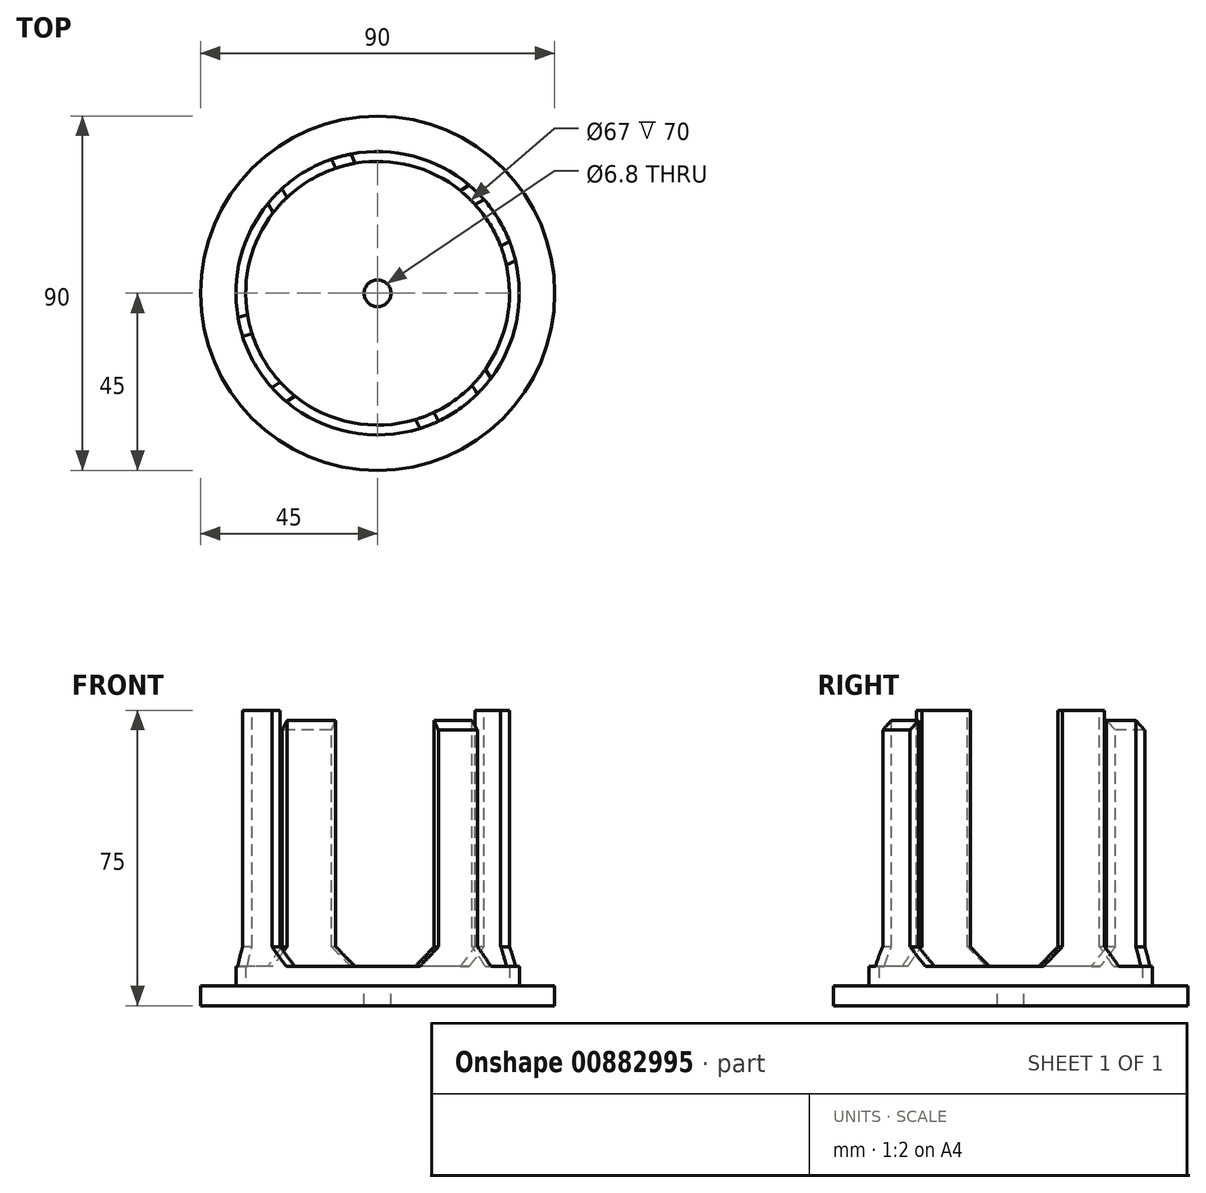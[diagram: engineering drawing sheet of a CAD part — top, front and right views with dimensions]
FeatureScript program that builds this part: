
annotation { "Feature Type Name" : "Feature", "Feature Type Description" : "" }
export const myFeature = defineFeature(function(context is Context, id is Id, definition is map)
    precondition{}
    {
        {
            var Q0;
            Q0=qCreatedBy(makeId("Top.planeOp"),FACE);
            var sketch = newSketch(context, id + "F0", { "sketchPlane" : qUnion([Q0])});
            skCircle(sketch, "E0", {"center": v(0, 0) * mm, "radius": 45 * mm});
            skSolve(sketch);
        }
        {
            var Q0;
            Q0 = qSketchRegion(id + "F0", true);
            extrude(context, id + "F1", {"entities" : qUnion([Q0]), "depth" : 5 * mm, "offsetDistance" : 25 * mm});
        }
        {
            var Q0;
            Q0=makeQuery(id+"F1.opExtrude","CAP_FACE",FACE,{"disambiguationData":[OSD([sQuery(id+"F0.wireOp",EDGE,"E0")])],"isStart":false});
            var sketch = newSketch(context, id + "F2", { "sketchPlane" : qUnion([Q0])});
            skCircle(sketch, "E1", {"center": v(0, 0) * mm, "radius": 36 * mm});
            skCircle(sketch, "E2", {"center": v(0, 0) * mm, "radius": 33.5 * mm});
            skSolve(sketch);
        }
        {
            var Q0;
            Q0=makeQuery(id+"F2.imprint","IMPRINT",FACE,{"disambiguationData":[TD([[makeQuery(id+"F2.imprint","IMPRINT",EDGE,{"derivedFrom":sQuery(id+"F2.wireOp",EDGE,"E1")}),1.0]])]});
            extrude(context, id + "F3", {"entities" : qUnion([Q0]), "operationType" : NewBodyOperationType.ADD, "depth" : 70 * mm, "offsetDistance" : 25 * mm});
        }
        {
            var Q0;
            Q0=makeQuery(id+"F3.opExtrude","CAP_FACE",FACE,{"disambiguationData":[OSD([sQuery(id+"F2.wireOp",EDGE,"E1"),sQuery(id+"F2.wireOp",EDGE,"E2")])],"isStart":false});
            var sketch = newSketch(context, id + "F4", { "sketchPlane" : qUnion([Q0])});
            skLineSegment(sketch, "E3", {"start": v(-24.29, 26.57) * mm, "end": v(-23, 24.36) * mm});
            skLineSegment(sketch, "E4", {"start": v(-11.71, 34.04) * mm, "end": v(-10.63, 31.77) * mm});
            skLineSegment(sketch, "E5", {"start": v(24, -23.38) * mm, "end": v(25.35, -25.56) * mm});
            skLineSegment(sketch, "E6", {"start": v(14.33, -30.28) * mm, "end": v(15.46, -32.51) * mm});
            skLineSegment(sketch, "E7", {"start": v(24.8, 22.52) * mm, "end": v(26.98, 23.84) * mm});
            skLineSegment(sketch, "E8", {"start": v(31.27, 12.01) * mm, "end": v(33.52, 13.12) * mm});
            skLineSegment(sketch, "E9", {"start": v(-31.88, -10.28) * mm, "end": v(-34.28, -11) * mm});
            skLineSegment(sketch, "E10", {"start": v(-24.74, -22.59) * mm, "end": v(-26.84, -24) * mm});
            skSolve(sketch);
        }
        {
            var Q0;
            {var subQ0=sQuery(id+"F4.wireOp",EDGE,"E3");Q0=makeQuery(id+"F4.imprint","IMPRINT",FACE,{"disambiguationData":[TD([[makeQuery(id+"F4.imprint","IMPRINT",EDGE,{"derivedFrom":subQ0}),-1.0]])]});}
            var Q1;
            {var subQ0=sQuery(id+"F4.wireOp",EDGE,"E4");Q1=makeQuery(id+"F4.imprint","IMPRINT",FACE,{"disambiguationData":[TD([[makeQuery(id+"F4.imprint","IMPRINT",EDGE,{"derivedFrom":subQ0}),1.0]])]});}
            var Q2;
            {var subQ0=sQuery(id+"F4.wireOp",EDGE,"E5");Q2=makeQuery(id+"F4.imprint","IMPRINT",FACE,{"disambiguationData":[TD([[makeQuery(id+"F4.imprint","IMPRINT",EDGE,{"derivedFrom":subQ0}),1.0]])]});}
            var Q3;
            {var subQ0=sQuery(id+"F4.wireOp",EDGE,"E6");Q3=makeQuery(id+"F4.imprint","IMPRINT",FACE,{"disambiguationData":[TD([[makeQuery(id+"F4.imprint","IMPRINT",EDGE,{"derivedFrom":subQ0}),-1.0]])]});}
            extrude(context, id + "F5", {"entities" : qUnion([Q0, Q1, Q2, Q3]), "operationType" : NewBodyOperationType.REMOVE, "oppositeDirection" : true, "depth" : 65 * mm, "offsetDistance" : 25 * mm});
        }
        {
            var Q0;
            Q0=makeQuery(id+"F3.boolean.opBoolean","SPLIT",FACE,{"disambiguationData":[TD([makeQuery(id+"F3.opExtrude","SWEPT_FACE",FACE,{"disambiguationData":[OSD([sQuery(id+"F2.wireOp",EDGE,"E2")])]})])],"derivedFrom":makeQuery(id+"F1.opExtrude","CAP_FACE",FACE,{"disambiguationData":[OSD([sQuery(id+"F0.wireOp",EDGE,"E0")])],"isStart":false})});
            var sketch = newSketch(context, id + "F6", { "sketchPlane" : qUnion([Q0])});
            skCircle(sketch, "E11", {"center": v(0, 0) * mm, "radius": 3.4 * mm});
            skSolve(sketch);
        }
        {
            var Q0;
            Q0 = qSketchRegion(id + "F6", true);
            extrude(context, id + "F7", {"entities" : qUnion([Q0]), "operationType" : NewBodyOperationType.REMOVE, "endBound" : BoundingType.THROUGH_ALL, "oppositeDirection" : true, "depth" : 25 * mm, "offsetDistance" : 25 * mm});
        }
        {
            var Q0;
            {var subQ0=sQuery(id+"F2.wireOp",EDGE,"E1");Q0=makeQuery(id+"F5.boolean.opBoolean","SPLIT",EDGE,{"disambiguationData":[TD([makeQuery(id+"F5.opExtrude","SWEPT_FACE",FACE,{"disambiguationData":[OSD([sQuery(id+"F4.wireOp",EDGE,"E3")])]})])],"derivedFrom":makeQuery(id+"F3.opExtrude","CAP_EDGE",EDGE,{"disambiguationData":[OSD([subQ0])],"isStart":false})});}
            var Q1;
            {var subQ0=sQuery(id+"F2.wireOp",EDGE,"E1");Q1=makeQuery(id+"F5.boolean.opBoolean","SPLIT",EDGE,{"disambiguationData":[TD([makeQuery(id+"F5.opExtrude","SWEPT_FACE",FACE,{"disambiguationData":[OSD([sQuery(id+"F4.wireOp",EDGE,"E4")])]})])],"derivedFrom":makeQuery(id+"F3.opExtrude","CAP_EDGE",EDGE,{"disambiguationData":[OSD([subQ0])],"isStart":false})});}
            var Q2;
            {var subQ0=sQuery(id+"F2.wireOp",EDGE,"E1");Q2=makeQuery(id+"F5.boolean.opBoolean","SPLIT",EDGE,{"disambiguationData":[TD([makeQuery(id+"F5.opExtrude","SWEPT_FACE",FACE,{"disambiguationData":[OSD([sQuery(id+"F4.wireOp",EDGE,"E5")])]})])],"derivedFrom":makeQuery(id+"F3.opExtrude","CAP_EDGE",EDGE,{"disambiguationData":[OSD([subQ0])],"isStart":false})});}
            var Q3;
            {var subQ0=sQuery(id+"F2.wireOp",EDGE,"E1");Q3=makeQuery(id+"F5.boolean.opBoolean","SPLIT",EDGE,{"disambiguationData":[TD([makeQuery(id+"F5.opExtrude","SWEPT_FACE",FACE,{"disambiguationData":[OSD([sQuery(id+"F4.wireOp",EDGE,"E6")])]})])],"derivedFrom":makeQuery(id+"F3.opExtrude","CAP_EDGE",EDGE,{"disambiguationData":[OSD([subQ0])],"isStart":false})});}
            chamfer(context, id + "F8", {"entities" : qUnion([Q0, Q1, Q2, Q3]), "width" : 5 * mm, "tangentPropagation" : true});
        }
        {
            var Q0;
            Q0=makeQuery(id+"F5.boolean.opBoolean","COPY",EDGE,{"derivedFrom":makeQuery(id+"F5.opExtrude","CAP_EDGE",EDGE,{"disambiguationData":[OSD([sQuery(id+"F4.wireOp",EDGE,"E3")])],"isStart":false})});
            var Q1;
            Q1=makeQuery(id+"F5.boolean.opBoolean","COPY",EDGE,{"derivedFrom":makeQuery(id+"F5.opExtrude","CAP_EDGE",EDGE,{"disambiguationData":[OSD([sQuery(id+"F4.wireOp",EDGE,"E4")])],"isStart":false})});
            var Q2;
            Q2=makeQuery(id+"F5.boolean.opBoolean","COPY",EDGE,{"derivedFrom":makeQuery(id+"F5.opExtrude","CAP_EDGE",EDGE,{"disambiguationData":[OSD([sQuery(id+"F4.wireOp",EDGE,"E7")])],"isStart":false})});
            var Q3;
            Q3=makeQuery(id+"F5.boolean.opBoolean","COPY",EDGE,{"derivedFrom":makeQuery(id+"F5.opExtrude","CAP_EDGE",EDGE,{"disambiguationData":[OSD([sQuery(id+"F4.wireOp",EDGE,"E8")])],"isStart":false})});
            var Q4;
            Q4=makeQuery(id+"F5.boolean.opBoolean","COPY",EDGE,{"derivedFrom":makeQuery(id+"F5.opExtrude","CAP_EDGE",EDGE,{"disambiguationData":[OSD([sQuery(id+"F4.wireOp",EDGE,"E5")])],"isStart":false})});
            var Q5;
            Q5=makeQuery(id+"F5.boolean.opBoolean","COPY",EDGE,{"derivedFrom":makeQuery(id+"F5.opExtrude","CAP_EDGE",EDGE,{"disambiguationData":[OSD([sQuery(id+"F4.wireOp",EDGE,"E6")])],"isStart":false})});
            var Q6;
            Q6=makeQuery(id+"F5.boolean.opBoolean","COPY",EDGE,{"derivedFrom":makeQuery(id+"F5.opExtrude","CAP_EDGE",EDGE,{"disambiguationData":[OSD([sQuery(id+"F4.wireOp",EDGE,"E10")])],"isStart":false})});
            var Q7;
            Q7=makeQuery(id+"F5.boolean.opBoolean","COPY",EDGE,{"derivedFrom":makeQuery(id+"F5.opExtrude","CAP_EDGE",EDGE,{"disambiguationData":[OSD([sQuery(id+"F4.wireOp",EDGE,"E9")])],"isStart":false})});
            chamfer(context, id + "F9", {"entities" : qUnion([Q0, Q1, Q2, Q3, Q4, Q5, Q6, Q7]), "width" : 5 * mm, "tangentPropagation" : true});
        }
    });
